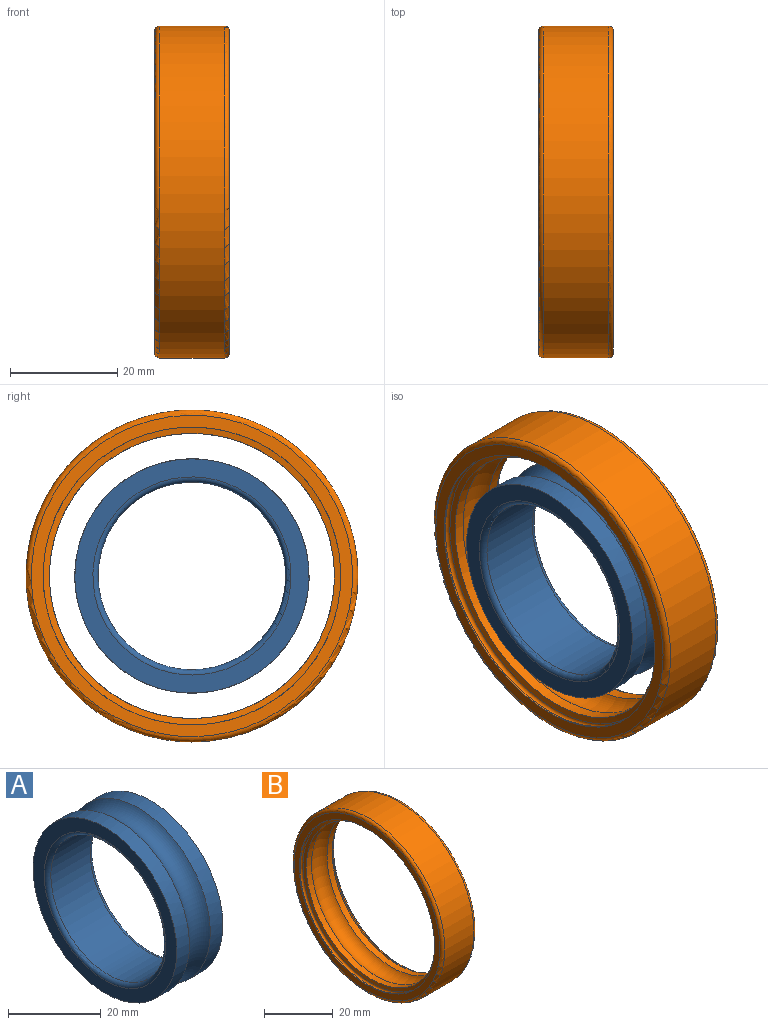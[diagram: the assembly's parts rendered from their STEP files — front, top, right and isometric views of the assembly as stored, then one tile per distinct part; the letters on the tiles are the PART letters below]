
ASSEMBLY  parts=2 mates=1
PART A: 8 faces, bbox 14x52.5x52.5 mm
  f0: torus R=18.5mm, axis (1,0,0), area 176.3mm2, adj f1,f2
  f1: cylinder r=17.5mm len=35mm, axis (1,0,0), area 1319.5mm2, adj f0,f3
  f2: plane 43.75x43.75mm, normal (-1,0,0), area 428mm2, adj f0,f4
  f3: torus R=18.5mm, axis (1,0,0), area 176.3mm2, adj f1,f5
  f4: cylinder r=21.88mm len=43.75mm, axis (1,0,0), area 525mm2, adj f2,f7
  f5: plane 43.75x43.75mm, normal (1,0,0), area 428.2mm2, adj f3,f6
  f6: cylinder r=21.88mm len=43.75mm, axis (1,0,0), area 525mm2, adj f5,f7
  f7: torus R=24.25mm, axis (1,0,0), area 965.4mm2, adj f4,f6
PART B: 14 faces, bbox 14x67.1x67.1 mm
  f0: cone r=0mm half-angle=80deg, axis (1,0,0), area 204.9mm2, adj f1,f2
  f1: torus R=27.8mm, axis (1,0,0), area 333.8mm2, adj f0,f3
  f2: cylinder r=26.62mm len=53.25mm, axis (1,0,0), area 353.3mm2, adj f0,f4
  f3: cylinder r=27.8mm len=55.61mm, axis (1,0,0), area 52.4mm2, adj f1,f5
  f4: torus R=24.25mm, axis (1,0,0), area 1282.6mm2, adj f2,f6
  f5: plane 60x60mm, normal (1,0,0), area 398.4mm2, adj f3,f7
  f6: cylinder r=26.62mm len=53.25mm, axis (1,0,0), area 353.3mm2, adj f4,f8
  f7: torus R=30mm, axis (1,0,0), area 302.4mm2, adj f5,f9
  f8: cone r=0mm half-angle=80deg, axis (-1,0,0), area 204.9mm2, adj f6,f10
  f9: cylinder r=31mm len=62mm, axis (1,0,0), area 2337.3mm2, adj f7,f11
  f10: torus R=27.8mm, axis (1,0,0), area 333.8mm2, adj f8,f12
  f11: torus R=30mm, axis (1,0,0), area 302.4mm2, adj f9,f13
  f12: cylinder r=27.8mm len=55.61mm, axis (1,0,0), area 52.4mm2, adj f10,f13
  f13: plane 60x60mm, normal (-1,0,0), area 398.8mm2, adj f11,f12
PLACE A rot(axis=(1,0,0),102.2deg) t=(0,0,0)mm
PLACE B at identity fixed
MATE revolute A.f0 <-> B.f0  axis (1,0,0) through (14,0,0)mm
